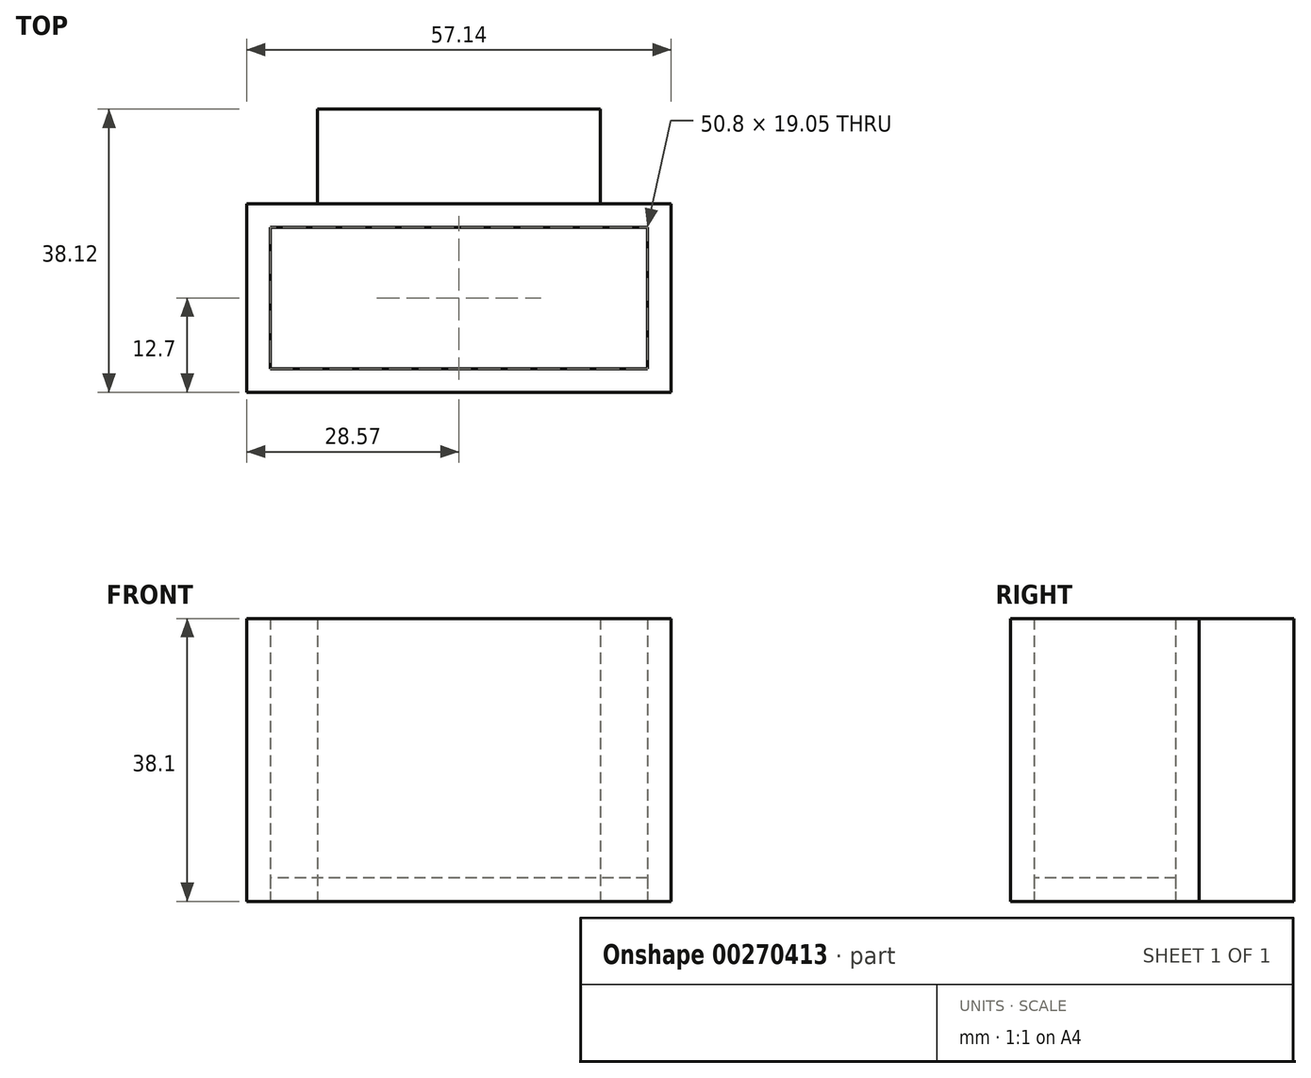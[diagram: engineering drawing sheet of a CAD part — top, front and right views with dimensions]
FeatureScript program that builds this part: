
annotation { "Feature Type Name" : "Feature", "Feature Type Description" : "" }
export const myFeature = defineFeature(function(context is Context, id is Id, definition is map)
    precondition{}
    {
        {
            var Q0;
            Q0=qCreatedBy(makeId("Top.planeOp"),FACE);
            var sketch = newSketch(context, id + "F0", { "sketchPlane" : qUnion([Q0])});
            skLineSegment(sketch, "E0.bottom", {"start": v(25.4, 9.53) * mm, "end": v(-25.4, 9.53) * mm});
            skLineSegment(sketch, "E0.top", {"start": v(25.4, -9.52) * mm, "end": v(-25.4, -9.52) * mm});
            skLineSegment(sketch, "E0.left", {"start": v(25.4, 9.53) * mm, "end": v(25.4, -9.52) * mm});
            skLineSegment(sketch, "E0.right", {"start": v(-25.4, 9.53) * mm, "end": v(-25.4, -9.52) * mm});
            skPoint(sketch, "E0.middle", {"position": v(0, 0) * mm});
            skLineSegment(sketch, "E1.bottom", {"start": v(28.58, 12.7) * mm, "end": v(-28.58, 12.7) * mm});
            skLineSegment(sketch, "E1.top", {"start": v(28.58, -12.7) * mm, "end": v(-28.58, -12.7) * mm});
            skLineSegment(sketch, "E1.left", {"start": v(28.58, 12.7) * mm, "end": v(28.58, -12.7) * mm});
            skLineSegment(sketch, "E1.right", {"start": v(-28.58, 12.7) * mm, "end": v(-28.58, -12.7) * mm});
            skLineSegment(sketch, "E2", {"start": v(0, 12.7) * mm, "end": v(0, 25.4) * mm});
            skLineSegment(sketch, "E3.bottom", {"start": v(19.05, 25.42) * mm, "end": v(-19.05, 25.42) * mm});
            skLineSegment(sketch, "E3.top", {"start": v(19.05, 12.68) * mm, "end": v(-19.05, 12.68) * mm});
            skLineSegment(sketch, "E3.left", {"start": v(19.05, 25.42) * mm, "end": v(19.05, 12.68) * mm});
            skLineSegment(sketch, "E3.right", {"start": v(-19.05, 25.42) * mm, "end": v(-19.05, 12.68) * mm});
            skPoint(sketch, "E3.middle", {"position": v(0, 19.05) * mm});
            skSolve(sketch);
        }
        {
            var Q0;
            Q0=makeQuery(id+"F0.imprint","IMPRINT",FACE,{"disambiguationData":[TD([[makeQuery(id+"F0.imprint","IMPRINT",EDGE,{"derivedFrom":sQuery(id+"F0.wireOp",EDGE,"E0.bottom")}),-1.0]])]});
            var Q1;
            {var subQ1=sQuery(id+"F0.wireOp",EDGE,"E3.bottom");Q1=makeQuery(id+"F0.imprint","IMPRINT",FACE,{"disambiguationData":[TD([[makeQuery(id+"F0.imprint","IMPRINT",EDGE,{"derivedFrom":subQ1}),1.0]])]});}
            extrude(context, id + "F1", {"entities" : qUnion([Q0, Q1]), "depth" : 38.1 * mm});
        }
        {
            var Q0;
            Q0=makeQuery(id+"F0.imprint","IMPRINT",FACE,{"disambiguationData":[TD([[makeQuery(id+"F0.imprint","IMPRINT",EDGE,{"derivedFrom":sQuery(id+"F0.wireOp",EDGE,"E0.bottom")}),1.0]])]});
            extrude(context, id + "F2", {"entities" : qUnion([Q0]), "depth" : 3.17 * mm});
        }
    });
